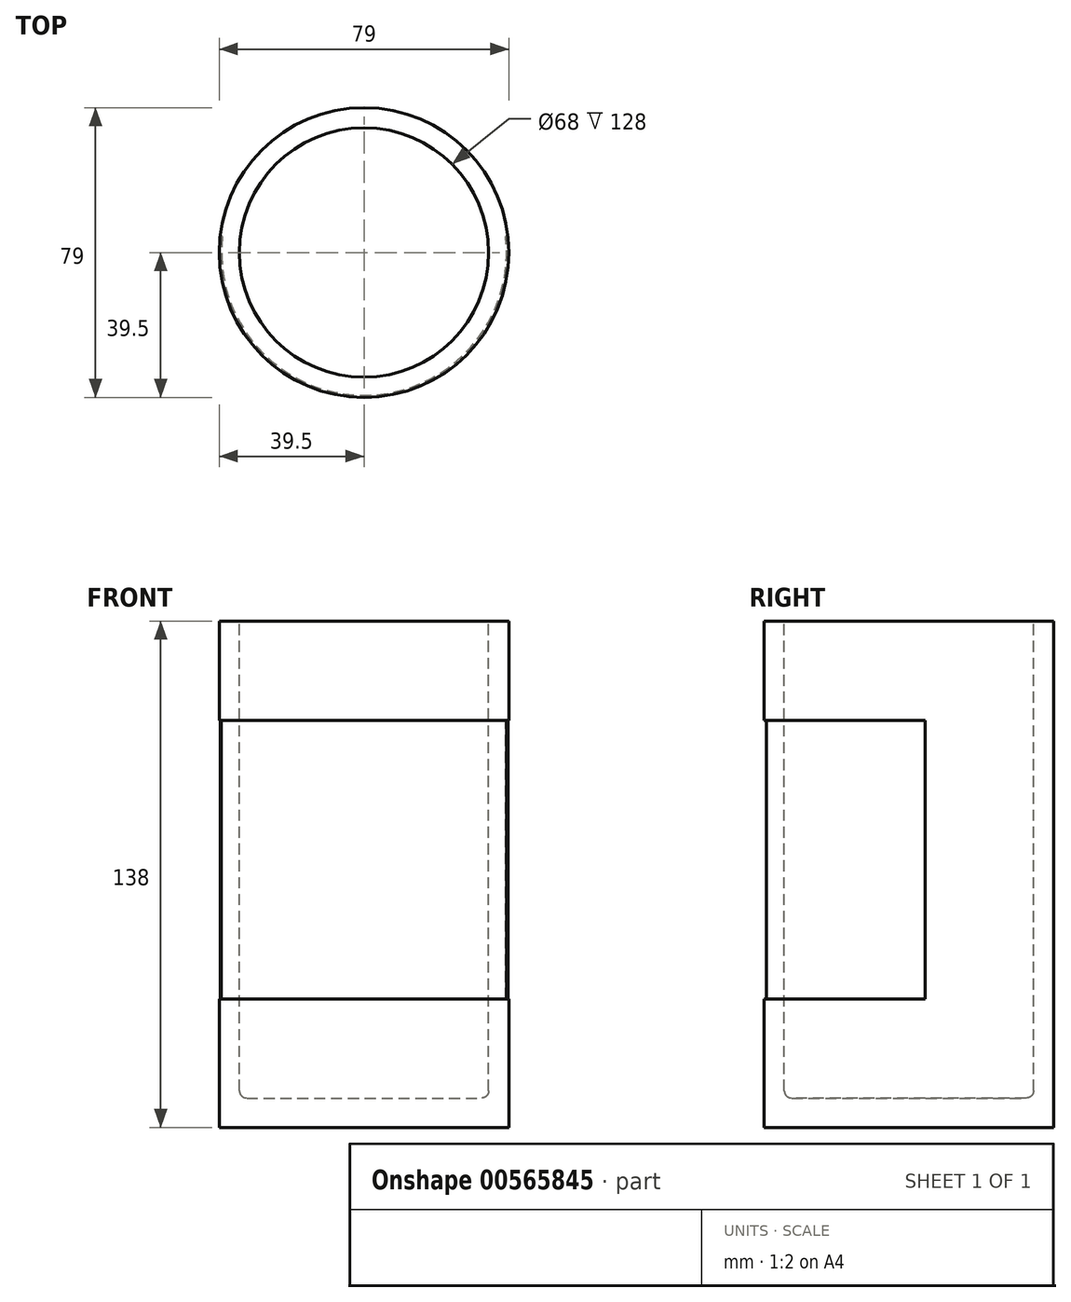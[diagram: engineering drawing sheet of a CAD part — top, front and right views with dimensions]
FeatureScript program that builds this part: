
annotation { "Feature Type Name" : "Feature", "Feature Type Description" : "" }
export const myFeature = defineFeature(function(context is Context, id is Id, definition is map)
    precondition{}
    {
        {
            var Q0;
            Q0=qCreatedBy(makeId("Top.planeOp"),FACE);
            var sketch = newSketch(context, id + "F0", { "sketchPlane" : qUnion([Q0])});
            skCircle(sketch, "E0", {"center": v(0, 0) * mm, "radius": 39.5 * mm});
            skSolve(sketch);
        }
        {
            var Q0;
            Q0 = qSketchRegion(id + "F0", true);
            extrude(context, id + "F1", {"entities" : qUnion([Q0]), "depth" : 138 * mm, "offsetDistance" : 25 * mm});
        }
        {
            var Q0;
            Q0=qCreatedBy(makeId("Front.planeOp"),FACE);
            var sketch = newSketch(context, id + "F2", { "sketchPlane" : qUnion([Q0])});
            skLineSegment(sketch, "E1", {"start": v(-34, 138) * mm, "end": v(-34, 8) * mm});
            skLineSegment(sketch, "E2", {"start": v(-34, 8) * mm, "end": v(0, 8) * mm});
            skLineSegment(sketch, "E3", {"start": v(0, 8) * mm, "end": v(0, 138) * mm});
            skLineSegment(sketch, "E4", {"start": v(0, 138) * mm, "end": v(-34, 138) * mm});
            skLineSegment(sketch, "E5.0", {"start": v(-39.5, 138) * mm, "end": v(39.5, 138) * mm, "construction": true});
            skLineSegment(sketch, "E6", {"start": v(0, 73) * mm, "end": v(36.9, 73) * mm, "construction": true});
            skSolve(sketch);
        }
        {
            var Q0;
            Q0 = qSketchRegion(id + "F2", true);
            var Q1;
            Q1=sQuery(id+"F2.wireOp",EDGE,"E3");
            revolve(context, id + "F3", {"operationType" : NewBodyOperationType.REMOVE, "entities" : qUnion([Q0]), "axis" : qUnion([Q1]), "revolveType" : RevolveType.FULL, "oppositeDirection" : true});
        }
        {
            var Q0;
            Q0=qCreatedBy(makeId("Top.planeOp"),FACE);
            var Q1;
            Q1=sQuery(id+"F2.wireOp",VERTEX,"E6.start");
            cPlane(context, id + "F4", {"entities" : qUnion([Q0, Q1]), "cplaneType" : CPlaneType.PLANE_POINT, "offset" : 25 * mm, "width" : 150 * mm, "height" : 150 * mm});
        }
        {
            var Q0;
            Q0=qCreatedBy(id+"F4.planeOp",FACE);
            var sketch = newSketch(context, id + "F5", { "sketchPlane" : qUnion([Q0])});
            skArc(sketch, "E7.0", {"start": v(-39.25, 4.47) * mm, "mid": v(0, -39.5) * mm, "end": v(39.25, 4.47) * mm});
            skLineSegment(sketch, "E8", {"start": v(0, 0) * mm, "end": v(-39.25, 4.47) * mm, "construction": true});
            skLineSegment(sketch, "E9", {"start": v(0, 0) * mm, "end": v(39.25, 4.47) * mm, "construction": true});
            skLineSegment(sketch, "E10", {"start": v(0, 0) * mm, "end": v(0, -39.5) * mm, "construction": true});
            skLineSegment(sketch, "E11", {"start": v(-39.25, 4.47) * mm, "end": v(0, -39.5) * mm, "construction": true});
            skLineSegment(sketch, "E12", {"start": v(39.25, 4.47) * mm, "end": v(0, -39.5) * mm, "construction": true});
            skArc(sketch, "E13.0", {"start": v(-38.65, 4.4) * mm, "mid": v(0, -38.9) * mm, "end": v(38.65, 4.4) * mm});
            skLineSegment(sketch, "E14", {"start": v(-39.25, 4.47) * mm, "end": v(-38.65, 4.4) * mm});
            skLineSegment(sketch, "E15", {"start": v(38.65, 4.4) * mm, "end": v(39.25, 4.47) * mm});
            skSolve(sketch);
        }
        {
            var Q0;
            Q0 = qSketchRegion(id + "F5", true);
            extrude(context, id + "F6", {"entities" : qUnion([Q0]), "operationType" : NewBodyOperationType.REMOVE, "endBound" : BoundingType.SYMMETRIC, "oppositeDirection" : true, "depth" : 76 * mm, "offsetDistance" : 25 * mm});
        }
        {
            var Q0;
            Q0=makeQuery(id+"F6.boolean.opBoolean","COPY",EDGE,{"derivedFrom":makeQuery(id+"F6.opExtrude","CAP_EDGE",EDGE,{"disambiguationData":[OSD([sQuery(id+"F5.wireOp",EDGE,"E13.0")])],"isStart":true})});
            fillet(context, id + "F7", {"entities" : qUnion([Q0]), "radius" : .6 * mm, "tangentPropagation" : true, "allowEdgeOverflow" : false});
        }
        {
            var Q0;
            Q0=makeQuery(id+"F3.boolean.opBoolean","COPY",EDGE,{"derivedFrom":makeQuery(id+"F3.opRevolve","SWEPT_EDGE",EDGE,{"disambiguationData":[OSD([sQuery(id+"F2.wireOp",EDGE,"E1"),sQuery(id+"F2.wireOp",EDGE,"E2")])]})});
            var Q1;
            Q1=makeQuery(id+"F3.boolean.opBoolean","COPY",EDGE,{"derivedFrom":makeQuery(id+"F3.opRevolve","SWEPT_EDGE",EDGE,{"disambiguationData":[OSD([sQuery(id+"F2.wireOp",EDGE,"E1"),sQuery(id+"F2.wireOp",EDGE,"E4")])]})});
            fillet(context, id + "F8", {"entities" : qUnion([Q0, Q1]), "radius" : 2 * mm, "tangentPropagation" : true, "allowEdgeOverflow" : false});
        }
    });
